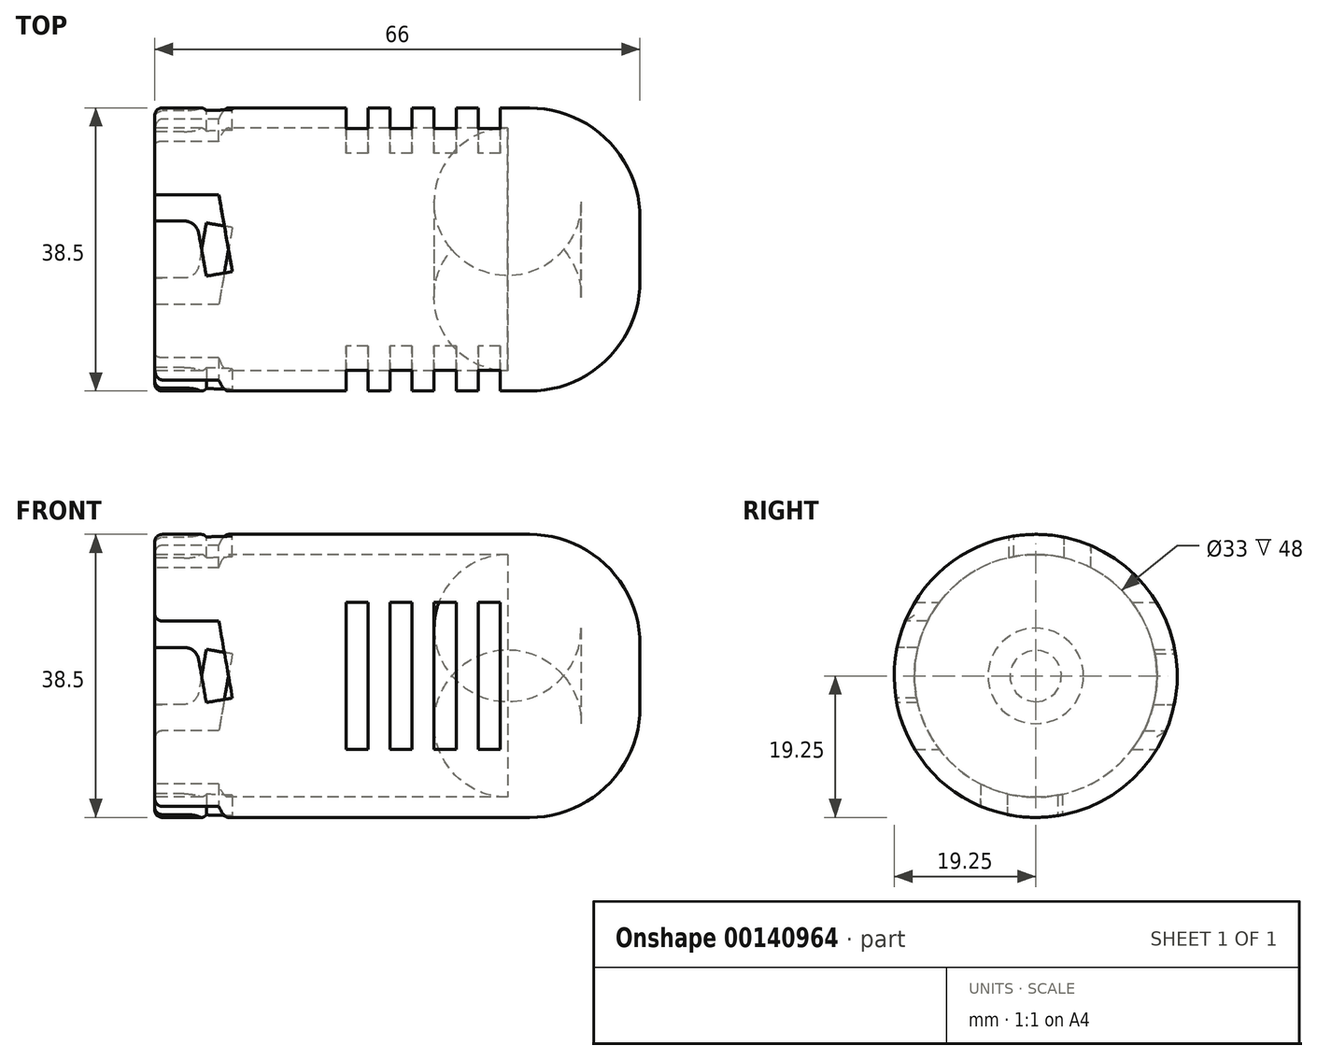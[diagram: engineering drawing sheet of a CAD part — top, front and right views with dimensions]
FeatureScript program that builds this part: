
annotation { "Feature Type Name" : "Feature", "Feature Type Description" : "" }
export const myFeature = defineFeature(function(context is Context, id is Id, definition is map)
    precondition{}
    {
        {
            var Q0;
            Q0=qCreatedBy(makeId("Right.planeOp"),FACE);
            var sketch = newSketch(context, id + "F0", { "sketchPlane" : qUnion([Q0])});
            skCircle(sketch, "E0", {"center": v(0, 0) * mm, "radius": 19.25 * mm});
            skSolve(sketch);
        }
        {
            var Q0;
            Q0=qSketchRegion(id+"F0",true);
            extrude(context, id + "F1", {"entities" : qUnion([Q0]), "depth" : 1 * mm});
        }
        {
            var Q0;
            Q0=makeQuery(id+"F1.opExtrude","CAP_FACE",FACE,{"disambiguationData":[OSD([sQuery(id+"F0.wireOp",EDGE,"E0")])],"isStart":true});
            var sketch = newSketch(context, id + "F2", { "sketchPlane" : qUnion([Q0])});
            skCircle(sketch, "E1", {"center": v(0, 0) * mm, "radius": 19.25 * mm});
            skSolve(sketch);
        }
        {
            var Q0;
            Q0=qSketchRegion(id+"F2",true);
            extrude(context, id + "F3", {"entities" : qUnion([Q0]), "operationType" : NewBodyOperationType.ADD, "depth" : 65 * mm});
        }
        {
            var Q0;
            Q0=makeQuery(id+"F3.opExtrude","CAP_FACE",FACE,{"disambiguationData":[OSD([sQuery(id+"F2.wireOp",EDGE,"E1")])],"isStart":false});
            var sketch = newSketch(context, id + "F4", { "sketchPlane" : qUnion([Q0])});
            skCircle(sketch, "E2", {"center": v(0, 0) * mm, "radius": 16.5 * mm});
            skSolve(sketch);
        }
        {
            var Q0;
            Q0=qCreatedBy(makeId("Top.planeOp"),FACE);
            cPlane(context, id + "F5", {"entities" : qUnion([Q0]), "cplaneType" : CPlaneType.OFFSET, "offset" : 20 * mm, "width" : 150 * mm, "height" : 150 * mm});
        }
        {
            var Q0;
            Q0=qCreatedBy(id+"F5.planeOp",FACE);
            var sketch = newSketch(context, id + "F6", { "sketchPlane" : qUnion([Q0])});
            skLineSegment(sketch, "E3", {"start": v(-65, 7.47) * mm, "end": v(-59.3, 7.47) * mm});
            skLineSegment(sketch, "E4", {"start": v(-65, 3.87) * mm, "end": v(-59.3, 3.87) * mm});
            skLineSegment(sketch, "E5", {"start": v(-65, 7.47) * mm, "end": v(-65, 3.87) * mm});
            skLineSegment(sketch, "E6", {"start": v(-59.3, 3.87) * mm, "end": v(-57.99, -3.63) * mm});
            skLineSegment(sketch, "E7", {"start": v(-54.44, -3) * mm, "end": v(-56.29, 7.47) * mm});
            skLineSegment(sketch, "E8", {"start": v(-59.3, 7.47) * mm, "end": v(-56.29, 7.47) * mm});
            skLineSegment(sketch, "E9", {"start": v(-54.44, -3) * mm, "end": v(-57.99, -3.63) * mm});
            skSolve(sketch);
        }
        {
            var Q0;
            Q0=makeQuery(id+"F6.imprint","IMPRINT",FACE,{"disambiguationData":[TD([[makeQuery(id+"F6.imprint","IMPRINT",EDGE,{"derivedFrom":sQuery(id+"F6.wireOp",EDGE,"E3")}),-1.0]])]});
            extrude(context, id + "F7", {"entities" : qUnion([Q0]), "operationType" : NewBodyOperationType.REMOVE, "oppositeDirection" : true, "depth" : 25 * mm});
        }
        {
            var Q0;
            Q0=qCreatedBy(makeId("Top.planeOp"),FACE);
            cPlane(context, id + "F8", {"entities" : qUnion([Q0]), "cplaneType" : CPlaneType.OFFSET, "offset" : 20 * mm, "oppositeDirection" : true, "width" : 150 * mm, "height" : 150 * mm});
        }
        {
            var Q0;
            Q0=qCreatedBy(id+"F8.planeOp",FACE);
            var sketch = newSketch(context, id + "F9", { "sketchPlane" : qUnion([Q0])});
            skLineSegment(sketch, "E10", {"start": v(-65, -7.47) * mm, "end": v(-59.3, -7.47) * mm});
            skLineSegment(sketch, "E11", {"start": v(-65, -7.47) * mm, "end": v(-65, -3.87) * mm});
            skLineSegment(sketch, "E12", {"start": v(-65, -3.87) * mm, "end": v(-59.3, -3.87) * mm});
            skLineSegment(sketch, "E13", {"start": v(-59.3, -3.87) * mm, "end": v(-57.99, 3.63) * mm});
            skLineSegment(sketch, "E14", {"start": v(-57.99, 3.63) * mm, "end": v(-54.44, 3) * mm});
            skLineSegment(sketch, "E15", {"start": v(-59.3, -7.47) * mm, "end": v(-56.29, -7.47) * mm});
            skLineSegment(sketch, "E16", {"start": v(-56.29, -7.47) * mm, "end": v(-54.44, 3) * mm});
            skSolve(sketch);
        }
        {
            var Q0;
            Q0=makeQuery(id+"F9.imprint","IMPRINT",FACE,{"disambiguationData":[TD([[makeQuery(id+"F9.imprint","IMPRINT",EDGE,{"derivedFrom":sQuery(id+"F9.wireOp",EDGE,"E10")}),1.0]])]});
            extrude(context, id + "F10", {"entities" : qUnion([Q0]), "operationType" : NewBodyOperationType.REMOVE, "depth" : 8 * mm});
        }
        {
            var Q0;
            Q0=qCreatedBy(makeId("Front.planeOp"),FACE);
            cPlane(context, id + "F11", {"entities" : qUnion([Q0]), "cplaneType" : CPlaneType.OFFSET, "offset" : 20 * mm, "width" : 150 * mm, "height" : 150 * mm});
        }
        {
            var Q0;
            Q0=qCreatedBy(makeId("Front.planeOp"),FACE);
            cPlane(context, id + "F12", {"entities" : qUnion([Q0]), "cplaneType" : CPlaneType.OFFSET, "offset" : 20 * mm, "oppositeDirection" : true, "width" : 150 * mm, "height" : 150 * mm});
        }
        {
            var Q0;
            Q0=qCreatedBy(id+"F12.planeOp",FACE);
            var sketch = newSketch(context, id + "F13", { "sketchPlane" : qUnion([Q0])});
            skLineSegment(sketch, "E17", {"start": v(-65, -7.47) * mm, "end": v(-59.3, -7.47) * mm});
            skLineSegment(sketch, "E18", {"start": v(-65, -7.47) * mm, "end": v(-65, -3.87) * mm});
            skLineSegment(sketch, "E19", {"start": v(-65, -3.87) * mm, "end": v(-59.3, -3.87) * mm});
            skLineSegment(sketch, "E20", {"start": v(-59.3, -3.87) * mm, "end": v(-57.99, 3.63) * mm});
            skLineSegment(sketch, "E21", {"start": v(-57.99, 3.63) * mm, "end": v(-54.44, 3) * mm});
            skLineSegment(sketch, "E22", {"start": v(-59.3, -7.47) * mm, "end": v(-56.29, -7.47) * mm});
            skLineSegment(sketch, "E23", {"start": v(-56.29, -7.47) * mm, "end": v(-54.44, 3) * mm});
            skSolve(sketch);
        }
        {
            var Q0;
            Q0=qSketchRegion(id+"F13",true);
            extrude(context, id + "F14", {"entities" : qUnion([Q0]), "operationType" : NewBodyOperationType.REMOVE, "depth" : 25 * mm});
        }
        {
            var Q0;
            Q0=qCreatedBy(id+"F11.planeOp",FACE);
            var sketch = newSketch(context, id + "F15", { "sketchPlane" : qUnion([Q0])});
            skLineSegment(sketch, "E24", {"start": v(-65, 7.47) * mm, "end": v(-59.3, 7.47) * mm});
            skLineSegment(sketch, "E25", {"start": v(-65, 3.87) * mm, "end": v(-59.3, 3.87) * mm});
            skLineSegment(sketch, "E26", {"start": v(-65, 7.47) * mm, "end": v(-65, 3.87) * mm});
            skLineSegment(sketch, "E27", {"start": v(-59.3, 3.87) * mm, "end": v(-57.99, -3.63) * mm});
            skLineSegment(sketch, "E28", {"start": v(-57.99, -3.63) * mm, "end": v(-54.44, -3) * mm});
            skLineSegment(sketch, "E29", {"start": v(-54.44, -3) * mm, "end": v(-56.29, 7.47) * mm});
            skLineSegment(sketch, "E30", {"start": v(-56.29, 7.47) * mm, "end": v(-59.3, 7.47) * mm});
            skSolve(sketch);
        }
        {
            var Q0;
            Q0=makeQuery(id+"F15.imprint","IMPRINT",FACE,{"disambiguationData":[TD([[makeQuery(id+"F15.imprint","IMPRINT",EDGE,{"derivedFrom":sQuery(id+"F15.wireOp",EDGE,"E24")}),-1.0]])]});
            extrude(context, id + "F16", {"entities" : qUnion([Q0]), "operationType" : NewBodyOperationType.REMOVE, "oppositeDirection" : true, "depth" : 25 * mm});
        }
        {
            var Q0;
            Q0=makeQuery(id+"F10.boolean.opBoolean","COPY",EDGE,{"derivedFrom":makeQuery(id+"F10.opExtrude","SWEPT_EDGE",EDGE,{"disambiguationData":[OSD([sQuery(id+"F9.wireOp",EDGE,"E12"),sQuery(id+"F9.wireOp",EDGE,"E13")])]})});
            var Q1;
            Q1=makeQuery(id+"F14.boolean.opBoolean","COPY",EDGE,{"derivedFrom":makeQuery(id+"F14.opExtrude","SWEPT_EDGE",EDGE,{"disambiguationData":[OSD([sQuery(id+"F13.wireOp",EDGE,"E19"),sQuery(id+"F13.wireOp",EDGE,"E20")])]})});
            var Q2;
            Q2=makeQuery(id+"F7.boolean.opBoolean","COPY",EDGE,{"derivedFrom":makeQuery(id+"F7.opExtrude","SWEPT_EDGE",EDGE,{"disambiguationData":[OSD([sQuery(id+"F6.wireOp",EDGE,"E4"),sQuery(id+"F6.wireOp",EDGE,"E6")])]})});
            var Q3;
            Q3=makeQuery(id+"F16.boolean.opBoolean","COPY",EDGE,{"derivedFrom":makeQuery(id+"F16.opExtrude","SWEPT_EDGE",EDGE,{"disambiguationData":[OSD([sQuery(id+"F15.wireOp",EDGE,"E25"),sQuery(id+"F15.wireOp",EDGE,"E27")])]})});
            fillet(context, id + "F17", {"entities" : qUnion([Q0, Q1, Q2, Q3]), "radius" : 2 * mm, "tangentPropagation" : true, "allowEdgeOverflow" : false});
        }
        {
            var Q0;
            Q0=makeQuery(id+"F1.opExtrude","CAP_EDGE",EDGE,{"disambiguationData":[OSD([sQuery(id+"F0.wireOp",EDGE,"E0")])],"isStart":false});
            fillet(context, id + "F18", {"entities" : qUnion([Q0]), "radius" : 15 * mm, "tangentPropagation" : true, "allowEdgeOverflow" : false});
        }
        {
            var Q0;
            Q0=qCreatedBy(id+"F12.planeOp",FACE);
            var sketch = newSketch(context, id + "F19", { "sketchPlane" : qUnion([Q0])});
            skLineSegment(sketch, "E31.bottom", {"start": v(-18, 10) * mm, "end": v(-21, 10) * mm});
            skLineSegment(sketch, "E31.top", {"start": v(-18, -10) * mm, "end": v(-21, -10) * mm});
            skLineSegment(sketch, "E31.left", {"start": v(-18, 10) * mm, "end": v(-18, -10) * mm});
            skLineSegment(sketch, "E31.right", {"start": v(-21, 10) * mm, "end": v(-21, -10) * mm});
            skLineSegment(sketch, "E32.bottom", {"start": v(-24, 10) * mm, "end": v(-27, 10) * mm});
            skLineSegment(sketch, "E32.top", {"start": v(-24, -10) * mm, "end": v(-27, -10) * mm});
            skLineSegment(sketch, "E32.left", {"start": v(-24, 10) * mm, "end": v(-24, -10) * mm});
            skLineSegment(sketch, "E32.right", {"start": v(-27, 10) * mm, "end": v(-27, -10) * mm});
            skLineSegment(sketch, "E33.bottom", {"start": v(-30, -10) * mm, "end": v(-33, -10) * mm});
            skLineSegment(sketch, "E33.top", {"start": v(-30, 10) * mm, "end": v(-33, 10) * mm});
            skLineSegment(sketch, "E33.left", {"start": v(-30, -10) * mm, "end": v(-30, 10) * mm});
            skLineSegment(sketch, "E33.right", {"start": v(-33, -10) * mm, "end": v(-33, 10) * mm});
            skPoint(sketch, "E34.oppositeSnap0", {"position": v(-31.5, -10) * mm});
            skLineSegment(sketch, "E34.bottom", {"start": v(-36, 10) * mm, "end": v(-39, 10) * mm});
            skLineSegment(sketch, "E34.top", {"start": v(-36, -10) * mm, "end": v(-39, -10) * mm});
            skLineSegment(sketch, "E34.left", {"start": v(-36, 10) * mm, "end": v(-36, -10) * mm});
            skLineSegment(sketch, "E34.right", {"start": v(-39, 10) * mm, "end": v(-39, -10) * mm});
            skSolve(sketch);
        }
        {
            var Q0;
            Q0=makeQuery(id+"F19.imprint","IMPRINT",FACE,{"disambiguationData":[TD([[makeQuery(id+"F19.imprint","IMPRINT",EDGE,{"derivedFrom":sQuery(id+"F19.wireOp",EDGE,"E31.bottom")}),1.0]])]});
            var Q1;
            Q1=makeQuery(id+"F19.imprint","IMPRINT",FACE,{"disambiguationData":[TD([[makeQuery(id+"F19.imprint","IMPRINT",EDGE,{"derivedFrom":sQuery(id+"F19.wireOp",EDGE,"E32.bottom")}),1.0]])]});
            var Q2;
            Q2=makeQuery(id+"F19.imprint","IMPRINT",FACE,{"disambiguationData":[TD([[makeQuery(id+"F19.imprint","IMPRINT",EDGE,{"derivedFrom":sQuery(id+"F19.wireOp",EDGE,"E33.bottom")}),-1.0]])]});
            var Q3;
            Q3=makeQuery(id+"F19.imprint","IMPRINT",FACE,{"disambiguationData":[TD([[makeQuery(id+"F19.imprint","IMPRINT",EDGE,{"derivedFrom":sQuery(id+"F19.wireOp",EDGE,"E34.bottom")}),1.0]])]});
            extrude(context, id + "F20", {"entities" : qUnion([Q0, Q1, Q2, Q3]), "operationType" : NewBodyOperationType.REMOVE, "depth" : 50 * mm});
        }
        {
            var Q0;
            {var subQ1=sQuery(id+"F2.wireOp",EDGE,"E1");Q0=makeQuery(id+"F14.boolean.opBoolean","SPLIT",EDGE,{"disambiguationData":[TD([makeQuery(id+"F14.opExtrude","SWEPT_FACE",FACE,{"disambiguationData":[OSD([sQuery(id+"F13.wireOp",EDGE,"E19")])]})])],"derivedFrom":makeQuery(id+"F10.boolean.opBoolean","SPLIT",EDGE,{"disambiguationData":[TD([makeQuery(id+"F10.opExtrude","SWEPT_FACE",FACE,{"disambiguationData":[OSD([sQuery(id+"F9.wireOp",EDGE,"E12")])]})])],"derivedFrom":makeQuery(id+"F3.opExtrude","CAP_EDGE",EDGE,{"disambiguationData":[OSD([subQ1])],"isStart":false})})});}
            var Q1;
            {var subQ0=makeQuery(id+"F10.opExtrude","SWEPT_FACE",FACE,{"disambiguationData":[OSD([sQuery(id+"F9.wireOp",EDGE,"E12")])]});var subQ1=sQuery(id+"F2.wireOp",EDGE,"E1");Q1=makeQuery(id+"F14.boolean.opBoolean","SPLIT",EDGE,{"disambiguationData":[TD([makeQuery(id+"F10.boolean.opBoolean","COPY",FACE,{"derivedFrom":subQ0})])],"derivedFrom":makeQuery(id+"F10.boolean.opBoolean","SPLIT",EDGE,{"disambiguationData":[TD([subQ0])],"derivedFrom":makeQuery(id+"F3.opExtrude","CAP_EDGE",EDGE,{"disambiguationData":[OSD([subQ1])],"isStart":false})})});}
            var Q2;
            {var subQ1=sQuery(id+"F2.wireOp",EDGE,"E1");Q2=makeQuery(id+"F16.boolean.opBoolean","SPLIT",EDGE,{"disambiguationData":[TD([makeQuery(id+"F16.opExtrude","SWEPT_FACE",FACE,{"disambiguationData":[OSD([sQuery(id+"F15.wireOp",EDGE,"E25")])]})])],"derivedFrom":makeQuery(id+"F10.boolean.opBoolean","SPLIT",EDGE,{"disambiguationData":[TD([makeQuery(id+"F7.boolean.opBoolean","COPY",FACE,{"derivedFrom":makeQuery(id+"F7.opExtrude","SWEPT_FACE",FACE,{"disambiguationData":[OSD([sQuery(id+"F6.wireOp",EDGE,"E4")])]})})])],"derivedFrom":makeQuery(id+"F3.opExtrude","CAP_EDGE",EDGE,{"disambiguationData":[OSD([subQ1])],"isStart":false})})});}
            var Q3;
            {var subQ0=makeQuery(id+"F7.boolean.opBoolean","COPY",FACE,{"derivedFrom":makeQuery(id+"F7.opExtrude","SWEPT_FACE",FACE,{"disambiguationData":[OSD([sQuery(id+"F6.wireOp",EDGE,"E4")])]})});var subQ1=sQuery(id+"F2.wireOp",EDGE,"E1");Q3=makeQuery(id+"F16.boolean.opBoolean","SPLIT",EDGE,{"disambiguationData":[TD([subQ0])],"derivedFrom":makeQuery(id+"F10.boolean.opBoolean","SPLIT",EDGE,{"disambiguationData":[TD([subQ0])],"derivedFrom":makeQuery(id+"F3.opExtrude","CAP_EDGE",EDGE,{"disambiguationData":[OSD([subQ1])],"isStart":false})})});}
            var Q4;
            {var subQ1=sQuery(id+"Ft8LlZTBeaotSWN_1.hole-0.sketch.wireOp",EDGE,"core_line_2");var subQ3=makeQuery(id+"F7.boolean.opBoolean","COPY",FACE,{"derivedFrom":makeQuery(id+"F7.opExtrude","SWEPT_FACE",FACE,{"disambiguationData":[OSD([sQuery(id+"F6.wireOp",EDGE,"E4")])]})});Q4=makeQuery(id+"F16.boolean.opBoolean","SPLIT",EDGE,{"disambiguationData":[TD([subQ3])],"derivedFrom":makeQuery(id+"F10.boolean.opBoolean","SPLIT",EDGE,{"disambiguationData":[TD([subQ3])],"derivedFrom":makeQuery(id+"Ft8LlZTBeaotSWN_1.hole-0.boolean.opBoolean","COPY",EDGE,{"derivedFrom":makeQuery(id+"Ft8LlZTBeaotSWN_1.hole-0.opRevolve","SWEPT_EDGE",EDGE,{"disambiguationData":[OSD([subQ1,sQuery(id+"Ft8LlZTBeaotSWN_1.hole-0.sketch.wireOp",EDGE,"core_line_3")])]})})})});}
            var Q5;
            {var subQ1=sQuery(id+"Ft8LlZTBeaotSWN_1.hole-0.sketch.wireOp",EDGE,"core_line_2");Q5=makeQuery(id+"F14.boolean.opBoolean","SPLIT",EDGE,{"disambiguationData":[TD([makeQuery(id+"F14.opExtrude","SWEPT_FACE",FACE,{"disambiguationData":[OSD([sQuery(id+"F13.wireOp",EDGE,"E19")])]})])],"derivedFrom":makeQuery(id+"F10.boolean.opBoolean","SPLIT",EDGE,{"disambiguationData":[TD([makeQuery(id+"F10.opExtrude","SWEPT_FACE",FACE,{"disambiguationData":[OSD([sQuery(id+"F9.wireOp",EDGE,"E12")])]})])],"derivedFrom":makeQuery(id+"Ft8LlZTBeaotSWN_1.hole-0.boolean.opBoolean","COPY",EDGE,{"derivedFrom":makeQuery(id+"Ft8LlZTBeaotSWN_1.hole-0.opRevolve","SWEPT_EDGE",EDGE,{"disambiguationData":[OSD([subQ1,sQuery(id+"Ft8LlZTBeaotSWN_1.hole-0.sketch.wireOp",EDGE,"core_line_3")])]})})})});}
            var Q6;
            {var subQ1=sQuery(id+"Ft8LlZTBeaotSWN_1.hole-0.sketch.wireOp",EDGE,"core_line_2");var subQ3=makeQuery(id+"F10.opExtrude","SWEPT_FACE",FACE,{"disambiguationData":[OSD([sQuery(id+"F9.wireOp",EDGE,"E12")])]});Q6=makeQuery(id+"F14.boolean.opBoolean","SPLIT",EDGE,{"disambiguationData":[TD([makeQuery(id+"F10.boolean.opBoolean","COPY",FACE,{"derivedFrom":subQ3})])],"derivedFrom":makeQuery(id+"F10.boolean.opBoolean","SPLIT",EDGE,{"disambiguationData":[TD([subQ3])],"derivedFrom":makeQuery(id+"Ft8LlZTBeaotSWN_1.hole-0.boolean.opBoolean","COPY",EDGE,{"derivedFrom":makeQuery(id+"Ft8LlZTBeaotSWN_1.hole-0.opRevolve","SWEPT_EDGE",EDGE,{"disambiguationData":[OSD([subQ1,sQuery(id+"Ft8LlZTBeaotSWN_1.hole-0.sketch.wireOp",EDGE,"core_line_3")])]})})})});}
            var Q7;
            {var subQ1=sQuery(id+"Ft8LlZTBeaotSWN_1.hole-0.sketch.wireOp",EDGE,"core_line_2");Q7=makeQuery(id+"F16.boolean.opBoolean","SPLIT",EDGE,{"disambiguationData":[TD([makeQuery(id+"F16.opExtrude","SWEPT_FACE",FACE,{"disambiguationData":[OSD([sQuery(id+"F15.wireOp",EDGE,"E25")])]})])],"derivedFrom":makeQuery(id+"F10.boolean.opBoolean","SPLIT",EDGE,{"disambiguationData":[TD([makeQuery(id+"F7.boolean.opBoolean","COPY",FACE,{"derivedFrom":makeQuery(id+"F7.opExtrude","SWEPT_FACE",FACE,{"disambiguationData":[OSD([sQuery(id+"F6.wireOp",EDGE,"E4")])]})})])],"derivedFrom":makeQuery(id+"Ft8LlZTBeaotSWN_1.hole-0.boolean.opBoolean","COPY",EDGE,{"derivedFrom":makeQuery(id+"Ft8LlZTBeaotSWN_1.hole-0.opRevolve","SWEPT_EDGE",EDGE,{"disambiguationData":[OSD([subQ1,sQuery(id+"Ft8LlZTBeaotSWN_1.hole-0.sketch.wireOp",EDGE,"core_line_3")])]})})})});}
            var Q8;
            Q8=makeQuery(id+"F10.boolean.opBoolean","COPY",EDGE,{"derivedFrom":makeQuery(id+"F10.opExtrude","SWEPT_EDGE",EDGE,{"disambiguationData":[OSD([sQuery(id+"F9.wireOp",EDGE,"E10"),sQuery(id+"F9.wireOp",EDGE,"E11")])]})});
            var Q9;
            Q9=makeQuery(id+"F10.boolean.opBoolean","COPY",EDGE,{"derivedFrom":makeQuery(id+"F10.opExtrude","SWEPT_EDGE",EDGE,{"disambiguationData":[OSD([sQuery(id+"F9.wireOp",EDGE,"E11"),sQuery(id+"F9.wireOp",EDGE,"E12")])]})});
            var Q10;
            Q10=makeQuery(id+"F14.boolean.opBoolean","COPY",EDGE,{"derivedFrom":makeQuery(id+"F14.opExtrude","SWEPT_EDGE",EDGE,{"disambiguationData":[OSD([sQuery(id+"F13.wireOp",EDGE,"E18"),sQuery(id+"F13.wireOp",EDGE,"E19")])]})});
            var Q11;
            Q11=makeQuery(id+"F14.boolean.opBoolean","COPY",EDGE,{"derivedFrom":makeQuery(id+"F14.opExtrude","SWEPT_EDGE",EDGE,{"disambiguationData":[OSD([sQuery(id+"F13.wireOp",EDGE,"E17"),sQuery(id+"F13.wireOp",EDGE,"E18")])]})});
            var Q12;
            Q12=makeQuery(id+"F7.boolean.opBoolean","COPY",EDGE,{"derivedFrom":makeQuery(id+"F7.opExtrude","SWEPT_EDGE",EDGE,{"disambiguationData":[OSD([sQuery(id+"F6.wireOp",EDGE,"E3"),sQuery(id+"F6.wireOp",EDGE,"E5")])]})});
            var Q13;
            Q13=makeQuery(id+"F7.boolean.opBoolean","COPY",EDGE,{"derivedFrom":makeQuery(id+"F7.opExtrude","SWEPT_EDGE",EDGE,{"disambiguationData":[OSD([sQuery(id+"F6.wireOp",EDGE,"E4"),sQuery(id+"F6.wireOp",EDGE,"E5")])]})});
            var Q14;
            Q14=makeQuery(id+"F16.boolean.opBoolean","COPY",EDGE,{"derivedFrom":makeQuery(id+"F16.opExtrude","SWEPT_EDGE",EDGE,{"disambiguationData":[OSD([sQuery(id+"F15.wireOp",EDGE,"E25"),sQuery(id+"F15.wireOp",EDGE,"E26")])]})});
            var Q15;
            Q15=makeQuery(id+"F16.boolean.opBoolean","COPY",EDGE,{"derivedFrom":makeQuery(id+"F16.opExtrude","SWEPT_EDGE",EDGE,{"disambiguationData":[OSD([sQuery(id+"F15.wireOp",EDGE,"E24"),sQuery(id+"F15.wireOp",EDGE,"E26")])]})});
            fillet(context, id + "F21", {"entities" : qUnion([Q0, Q1, Q2, Q3, Q4, Q5, Q6, Q7, Q8, Q9, Q10, Q11, Q12, Q13, Q14, Q15]), "radius" : 1 * mm, "tangentPropagation" : true, "allowEdgeOverflow" : false});
        }
        {
            var Q0;
            Q0 = qSketchRegion(id + "F4", true);
            extrude(context, id + "F22", {"entities" : qUnion([Q0]), "operationType" : NewBodyOperationType.REMOVE, "oppositeDirection" : true, "depth" : 58 * mm});
        }
        {
            var Q0;
            Q0=makeQuery(id+"F22.boolean.opBoolean","COPY",EDGE,{"derivedFrom":makeQuery(id+"F22.opExtrude","CAP_EDGE",EDGE,{"disambiguationData":[OSD([sQuery(id+"F4.wireOp",EDGE,"E2")])],"isStart":false})});
            fillet(context, id + "F23", {"entities" : qUnion([Q0]), "radius" : 10 * mm, "tangentPropagation" : true, "allowEdgeOverflow" : false});
        }
    });
